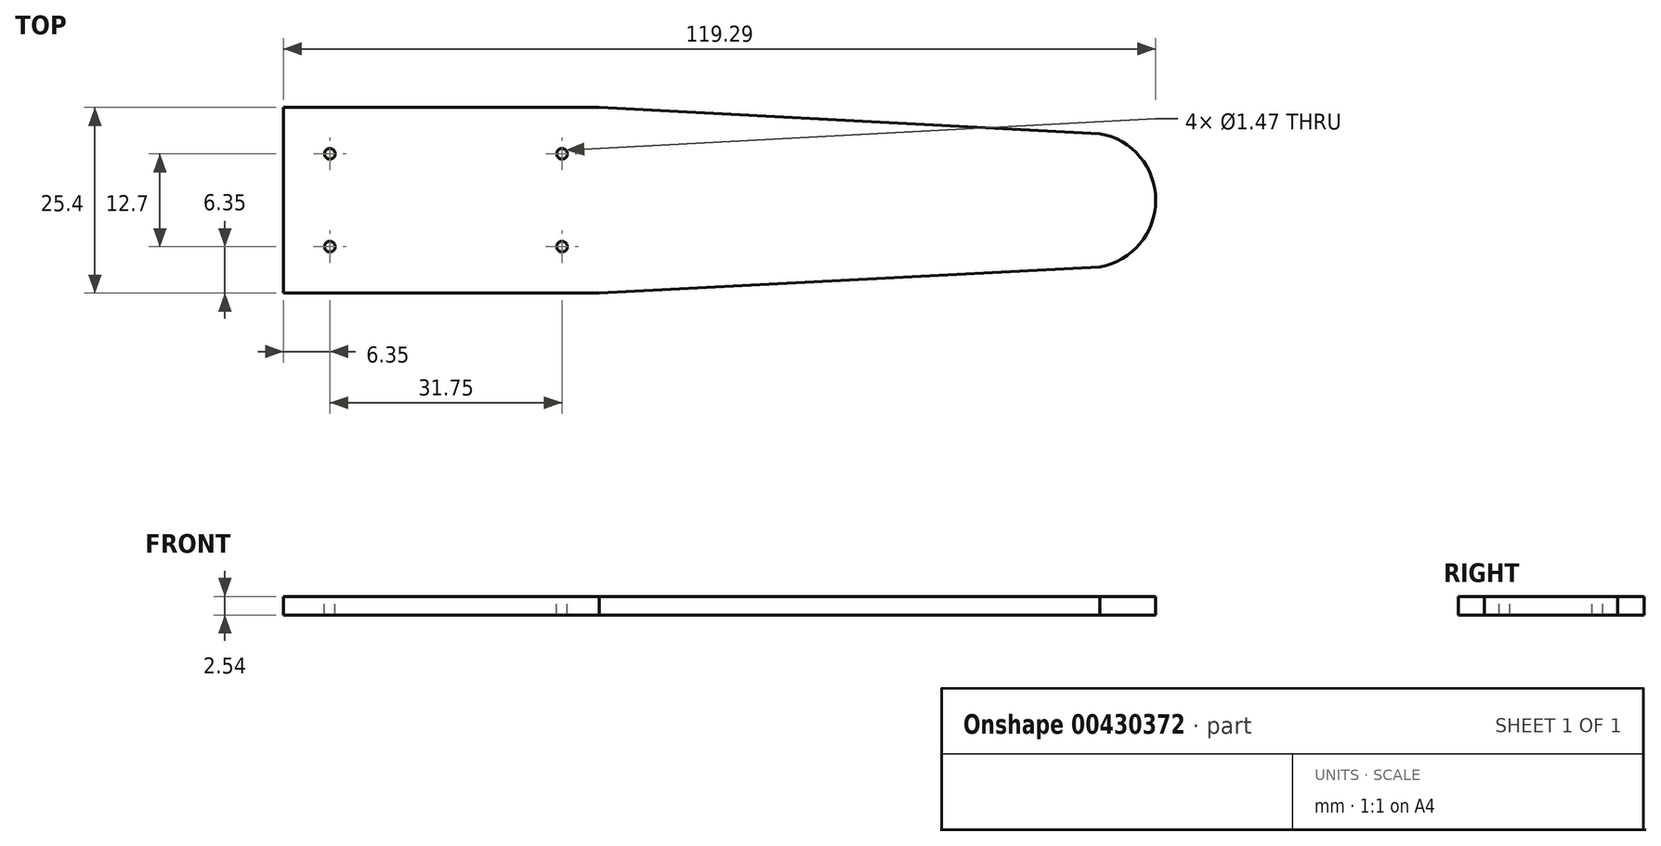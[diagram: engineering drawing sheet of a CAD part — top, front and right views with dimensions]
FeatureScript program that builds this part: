
annotation { "Feature Type Name" : "Feature", "Feature Type Description" : "" }
export const myFeature = defineFeature(function(context is Context, id is Id, definition is map)
    precondition{}
    {
        {
            var Q0;
            Q0=qCreatedBy(makeId("Top.planeOp"),FACE);
            var sketch = newSketch(context, id + "F0", { "sketchPlane" : qUnion([Q0])});
            skLineSegment(sketch, "E0", {"start": v(0, 0) * mm, "end": v(0, 25.4) * mm});
            skLineSegment(sketch, "E1", {"start": v(0, 25.4) * mm, "end": v(43.18, 25.4) * mm});
            skLineSegment(sketch, "E2", {"start": v(0, 0) * mm, "end": v(43.18, 0) * mm});
            skLineSegment(sketch, "E3", {"start": v(43.18, 0) * mm, "end": v(111.67, 3.59) * mm});
            skLineSegment(sketch, "E4", {"start": v(43.18, 25.4) * mm, "end": v(111.67, 21.81) * mm});
            skArc(sketch, "E5", {"start": v(111.67, 3.59) * mm, "mid": v(119.29, 12.7) * mm, "end": v(111.67, 21.81) * mm});
            skSolve(sketch);
        }
        {
            var Q0;
            Q0=makeQuery(id+"F0.imprint","IMPRINT",FACE,{"disambiguationData":[TD([[makeQuery(id+"F0.imprint","IMPRINT",EDGE,{"derivedFrom":sQuery(id+"F0.wireOp",EDGE,"E0")}),-1.0]])]});
            extrude(context, id + "F1", {"entities" : qUnion([Q0]), "depth" : 2.54 * mm});
        }
        {
            var Q0;
            Q0=makeQuery(id+"F1.opExtrude","CAP_FACE",FACE,{"disambiguationData":[OSD([sQuery(id+"F0.wireOp",EDGE,"E0"),sQuery(id+"F0.wireOp",EDGE,"E1"),sQuery(id+"F0.wireOp",EDGE,"E2"),sQuery(id+"F0.wireOp",EDGE,"E3"),sQuery(id+"F0.wireOp",EDGE,"E4"),sQuery(id+"F0.wireOp",EDGE,"E5")])],"isStart":false});
            var sketch = newSketch(context, id + "F2", { "sketchPlane" : qUnion([Q0])});
            skCircle(sketch, "E6", {"center": v(6.35, 19.05) * mm, "radius": 0.74 * mm});
            skCircle(sketch, "E7.0.1.0", {"center": v(6.35, 6.35) * mm, "radius": 0.74 * mm});
            skCircle(sketch, "E7.1.0.0", {"center": v(38.1, 19.05) * mm, "radius": 0.74 * mm});
            skCircle(sketch, "E7.1.1.0", {"center": v(38.1, 6.35) * mm, "radius": 0.74 * mm});
            skLineSegment(sketch, "E7.direction1", {"start": v(6.35, 19.05) * mm, "end": v(38.1, 19.05) * mm, "construction": true});
            skLineSegment(sketch, "E7.direction2", {"start": v(6.35, 19.05) * mm, "end": v(6.35, 6.35) * mm, "construction": true});
            skSolve(sketch);
        }
        {
            var Q0;
            Q0=makeQuery(id+"F2.imprint","IMPRINT",FACE,{"disambiguationData":[TD([[makeQuery(id+"F2.imprint","IMPRINT",EDGE,{"derivedFrom":sQuery(id+"F2.wireOp",EDGE,"E6")}),1.0]])]});
            var Q1;
            Q1=makeQuery(id+"F2.imprint","IMPRINT",FACE,{"disambiguationData":[TD([[makeQuery(id+"F2.imprint","IMPRINT",EDGE,{"derivedFrom":sQuery(id+"F2.wireOp",EDGE,"E7.0.1.0")}),1.0]])]});
            var Q2;
            Q2=makeQuery(id+"F2.imprint","IMPRINT",FACE,{"disambiguationData":[TD([[makeQuery(id+"F2.imprint","IMPRINT",EDGE,{"derivedFrom":sQuery(id+"F2.wireOp",EDGE,"E7.1.1.0")}),1.0]])]});
            var Q3;
            Q3=makeQuery(id+"F2.imprint","IMPRINT",FACE,{"disambiguationData":[TD([[makeQuery(id+"F2.imprint","IMPRINT",EDGE,{"derivedFrom":sQuery(id+"F2.wireOp",EDGE,"E7.1.0.0")}),1.0]])]});
            extrude(context, id + "F3", {"entities" : qUnion([Q0, Q1, Q2, Q3]), "operationType" : NewBodyOperationType.REMOVE, "oppositeDirection" : true, "depth" : 25.4 * mm});
        }
    });
